# Revit family: Linkeo Freestanding cabinets with single front door width 600
name_source: partatom
category: Equipement spécialisé
units: mm (PartAtom-declared; Revit-internal decimal feet)

## family parameters
Basée sur le plan de construction = Non
Cote de connecteur circulaire = Utiliser le diamètre
Couper avec des vides une fois chargée = Non
Numéro OmniClass = 23.85.05.17.11.14
Partagée = Oui
Point de calcul de pièce = Non
Titre OmniClass = Multimedia Broadcasting Equipment
Toujours verticalement = Oui
Type d'élément = Normal

## types (5) — shared parameters
Application class = EC002499
Avec porte frontale = Oui
Color = grey
Degree of protection IK = IK08
Degree of protection IP = IP20
Door symbol = Door symbol  Door 600mm
E-catalogue link = https://www.legrand.fr
Fabricant = Legrand
Front door material = glass
Function = Cabinet Linkeo2
Locking of the front door = One point
Material = Steel
Max load capacity = 400
Model = With permanent frame
Model width = 600 mm
Modular spacing = 19 inches
Mounting level = Front side
Number of doors = 1
Operating temperature = -25°C à 70°C
RAL Number = 7016
Rack location = 93 mm  [stored 0.305118 ft]
Storage temperature = -25°C à 70°C
Type of profile rail = Crank
Type of surface = Powder coating
Type of ventilation = None
Width (mm) = 610 mm  [stored 2.00131 ft]
With earthing = Oui
With roof plate = Oui
zero-valued in all types: Elévation par défaut

## per-type parameters (varying)
| type | Depth | Depth of the model (mm) | Distance of the aperture 1 | EAN | Height | Legrand part number | Number of height units | Type of horizontal uprights | Type of levelling feet | Type of vertical uprights | Usable height (mm) | Usable width (mm) |
| Cabinet Linkeo2 24U 600x600 | 630 mm  [stored 2.06693 ft] | 600 mm | 57 mm  [stored 0.187008 ft] | 3414971001503 | 1226 mm  [stored 4.02231 ft] | 646750 | 24 | Horizontal uprights for Linkeo freestanding cabinets  24U depth 600 | Levelling feet  600X600 | Vertical uprights for Linkeo freestanding cabinets  24U | 1081 mm  [stored 3.54659 ft] | 490 mm  [stored 1.60761 ft] |
| Cabinet Linkeo2 42U 600x800 | 830 mm  [stored 2.7231 ft] | 800 mm  [stored 2.62467 ft] | 257 mm  [stored 0.843176 ft] | 3414971001558 | 2026 mm | 646761 | 42 | Horizontal uprights for Linkeo freestanding cabinets  42U depth 800 | Levelling feet  600X800 | Vertical uprights for Linkeo freestanding cabinets  42U | 1881 mm  [stored 6.17126 ft] | 690 mm  [stored 2.26378 ft] |
| Cabinet Linkeo2 33U 600x600 | 630 mm  [stored 2.06693 ft] | 600 mm | 57 mm  [stored 0.187008 ft] | 3414971001527 | 1626 mm | 646755 | 33 | Horizontal uprights for Linkeo freestanding cabinets  33U depth 600 | Levelling feet  600X600 | Vertical uprights for Linkeo freestanding cabinets  33U | 1481 mm  [stored 4.85892 ft] | 490 mm  [stored 1.60761 ft] |
| Cabinet Linkeo2 42U 600x600 | 630 mm  [stored 2.06693 ft] | 600 mm | 57 mm  [stored 0.187008 ft] | 3414971001541 | 2026 mm | 646760 | 42 | Horizontal uprights for Linkeo freestanding cabinets  42U depth 600 | Levelling feet  600X600 | Vertical uprights for Linkeo freestanding cabinets  42U | 1881 mm  [stored 6.17126 ft] | 490 mm  [stored 1.60761 ft] |
| Cabinet Linkeo2 42U 600x1000 | 1030 mm  [stored 3.37927 ft] | 1000 mm  [stored 3.28084 ft] | 457 mm  [stored 1.49934 ft] | 3414971001565 | 2026 mm | 646762 | 42 | Horizontal uprights for Linkeo freestanding cabinets  42U depth 1000 | Levelling feet  600X1000 | Vertical uprights for Linkeo freestanding cabinets  42U | 1881 mm  [stored 6.17126 ft] | 890 mm  [stored 2.91995 ft] |

note: column(s) folded — value = type name in every type: BIM wording

note: [stored X ft] marks values corroborated as IEEE doubles in the binary element streams (Revit-internal decimal feet)
